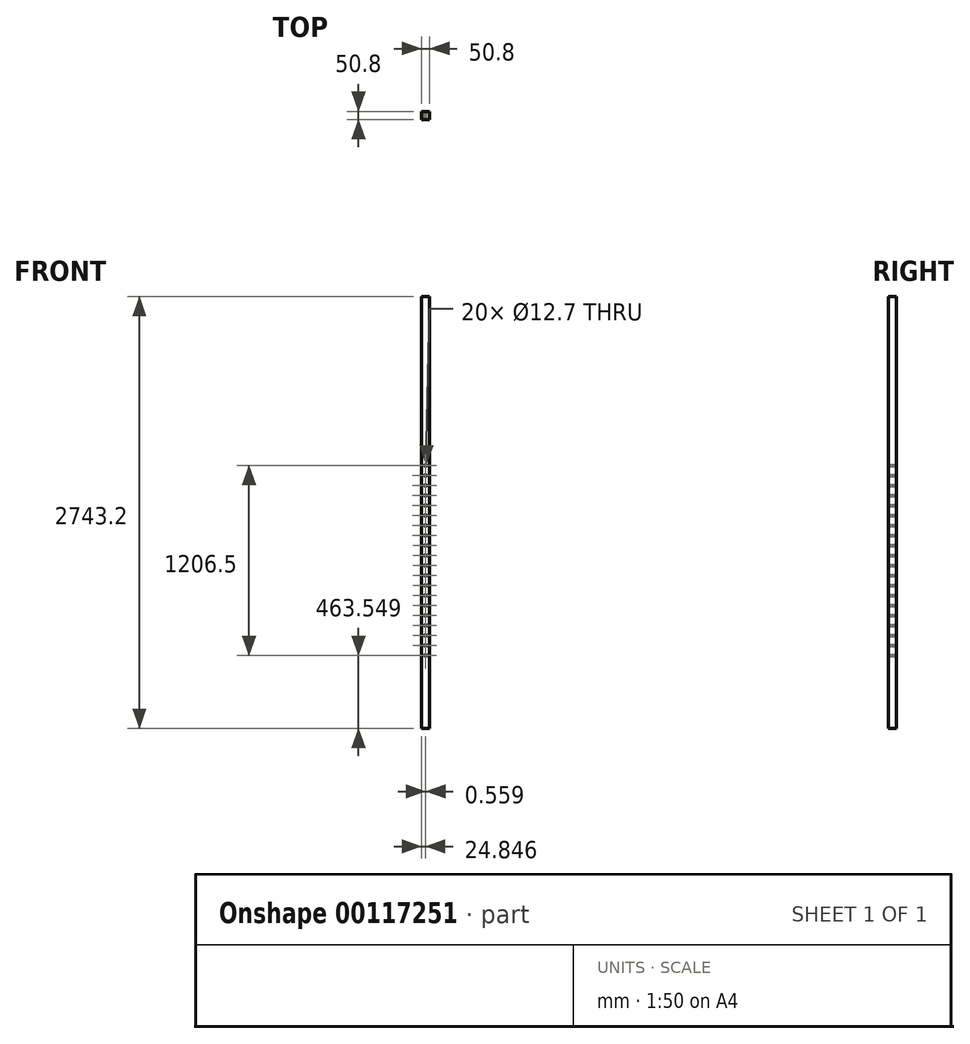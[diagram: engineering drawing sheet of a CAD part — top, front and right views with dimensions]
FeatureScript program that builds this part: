
annotation { "Feature Type Name" : "Feature", "Feature Type Description" : "" }
export const myFeature = defineFeature(function(context is Context, id is Id, definition is map)
    precondition{}
    {
        {
            var Q0;
            Q0=qCreatedBy(makeId("Front.planeOp"),FACE);
            var sketch = newSketch(context, id + "F0", { "sketchPlane" : qUnion([Q0])});
            skLineSegment(sketch, "E0", {"start": v(-83.36, -671.76) * mm, "end": v(-32.56, -671.76) * mm});
            skLineSegment(sketch, "E1", {"start": v(-32.56, -671.76) * mm, "end": v(-32.56, 2071.44) * mm});
            skLineSegment(sketch, "E2", {"start": v(-32.56, 2071.44) * mm, "end": v(-83.36, 2071.44) * mm});
            skLineSegment(sketch, "E3", {"start": v(-83.36, 2071.44) * mm, "end": v(-83.36, -671.76) * mm});
            skCircle(sketch, "E4", {"center": v(-57.96, -208.21) * mm, "radius": 6.35 * mm});
            skCircle(sketch, "E5", {"center": v(-57.96, -144.71) * mm, "radius": 6.35 * mm});
            skCircle(sketch, "E6", {"center": v(-57.96, -81.21) * mm, "radius": 6.35 * mm});
            skCircle(sketch, "E7", {"center": v(-57.96, -17.71) * mm, "radius": 6.35 * mm});
            skCircle(sketch, "E8", {"center": v(-57.96, 45.79) * mm, "radius": 6.35 * mm});
            skCircle(sketch, "E9", {"center": v(-57.96, 109.29) * mm, "radius": 6.35 * mm});
            skCircle(sketch, "E10", {"center": v(-57.96, 172.79) * mm, "radius": 6.35 * mm});
            skCircle(sketch, "E11", {"center": v(-57.96, 236.29) * mm, "radius": 6.35 * mm});
            skCircle(sketch, "E12", {"center": v(-57.96, 299.79) * mm, "radius": 6.35 * mm});
            skCircle(sketch, "E13", {"center": v(-57.96, 363.29) * mm, "radius": 6.35 * mm});
            skCircle(sketch, "E14", {"center": v(-57.96, 426.79) * mm, "radius": 6.35 * mm});
            skCircle(sketch, "E15", {"center": v(-57.96, 490.29) * mm, "radius": 6.35 * mm});
            skCircle(sketch, "E16", {"center": v(-58.51, 553.79) * mm, "radius": 6.35 * mm});
            skCircle(sketch, "E17", {"center": v(-58.51, 617.29) * mm, "radius": 6.35 * mm});
            skCircle(sketch, "E18", {"center": v(-58.51, 680.79) * mm, "radius": 6.35 * mm});
            skCircle(sketch, "E19", {"center": v(-58.51, 744.29) * mm, "radius": 6.35 * mm});
            skCircle(sketch, "E20", {"center": v(-58.51, 807.79) * mm, "radius": 6.35 * mm});
            skCircle(sketch, "E21", {"center": v(-58.51, 871.29) * mm, "radius": 6.35 * mm});
            skCircle(sketch, "E22", {"center": v(-58.51, 934.79) * mm, "radius": 6.35 * mm});
            skCircle(sketch, "E23", {"center": v(-58.51, 998.29) * mm, "radius": 6.35 * mm});
            skSolve(sketch);
        }
        {
            var Q0;
            Q0=makeQuery(id+"F0.imprint","IMPRINT",FACE,{"disambiguationData":[TD([[makeQuery(id+"F0.imprint","IMPRINT",EDGE,{"derivedFrom":sQuery(id+"F0.wireOp",EDGE,"E0")}),1.0]])]});
            extrude(context, id + "F1", {"entities" : qUnion([Q0]), "endBound" : BoundingType.SYMMETRIC, "depth" : 50.8 * mm});
        }
        {
            var Q0;
            Q0=makeQuery(id+"F0.imprint","IMPRINT",FACE,{"disambiguationData":[TD([[makeQuery(id+"F0.imprint","IMPRINT",EDGE,{"derivedFrom":sQuery(id+"F0.wireOp",EDGE,"E0")}),1.0]])]});
            extrude(context, id + "F2", {"entities" : qUnion([Q0]), "operationType" : NewBodyOperationType.ADD, "endBound" : BoundingType.SYMMETRIC, "depth" : 50.8 * mm});
        }
    });
